# Revit family: Site - Basketball Court - P - UH
name_source: partatom
category: Site
units: mm (PartAtom-declared; Revit-internal decimal feet)

## family parameters
Always vertical = Yes
Cut with Voids When Loaded = No
Part Type = Normal
Round Connector Dimension = Use Diameter
Shared = No
Work Plane-Based = No

## types (1)
- Basketball Court - Junior High (74'x42')
    Boundary Line = Basketball Court - Boundary Line
    Center Circle = Basketball Court - Center Circle
    Color Belt = Basketball Court - Color Belt
    Court Finish = Basketball Court - Interior Court Finish
    Court Length = 22555 mm
    Court Width = 12802 mm
    Freethrow Line Circle = Basketball Court - Freethrow Line Circle
    Key Depth = 4572 mm  [stored 15 ft]
    Key Width = 3658 mm
    Key/Shaded Lane = Basketball Court - Key/Shaded Lane
    Line Thickness = 13 mm
    Manufacturer = www.revitcomponents.com
    Model = Basketball Court
    Restraining Circle = Basketball Court - Restraining Circle
    Side/End Line Width = 203 mm
    Source = www.revitcomponents.com
    URL = www.revitcomponents.com

note: [stored X ft] marks values corroborated as IEEE doubles in the binary element streams (Revit-internal decimal feet)

## geometry (parser evidence)
native form markers: Sweep x1
no freeform markers — native parametric forms only
